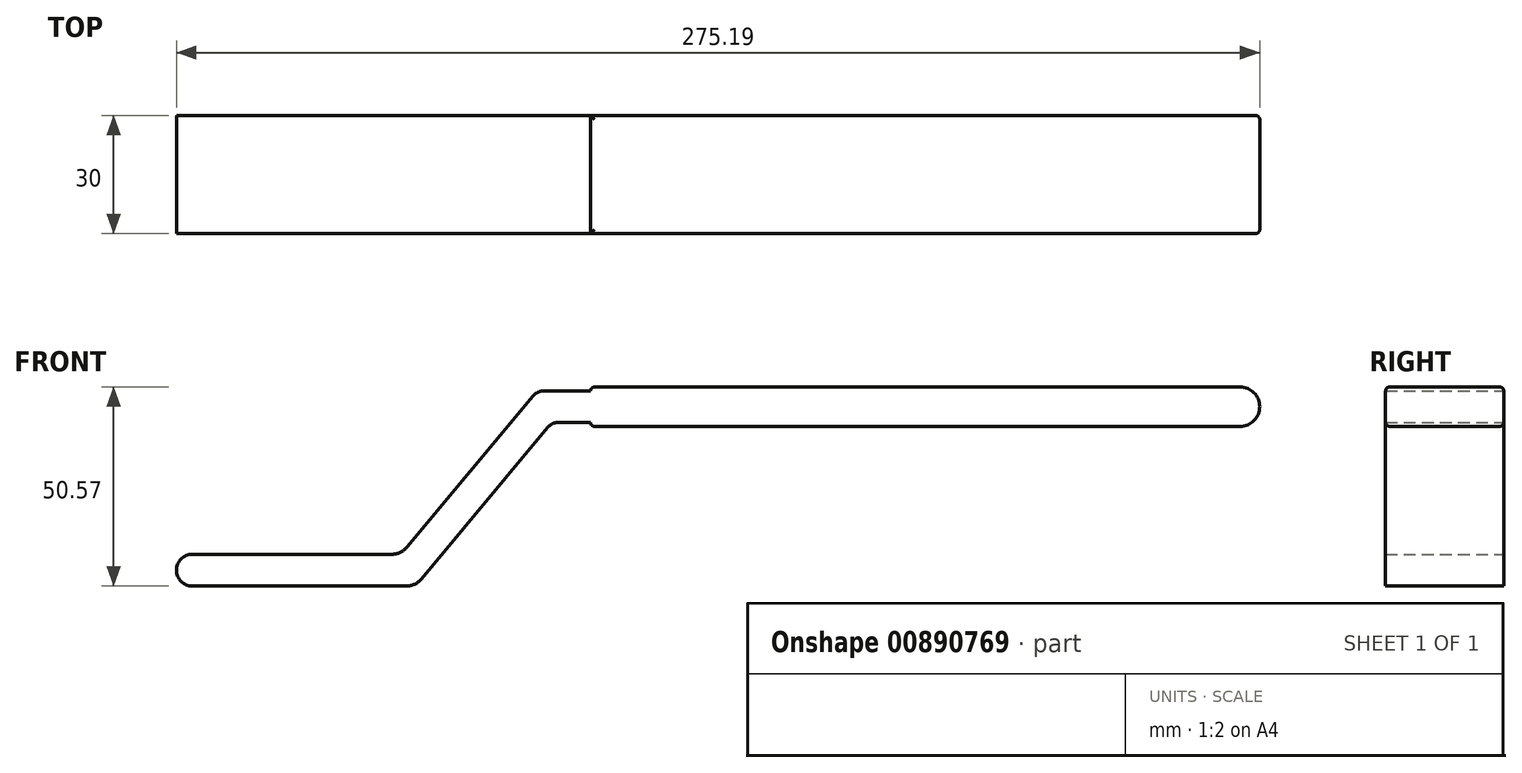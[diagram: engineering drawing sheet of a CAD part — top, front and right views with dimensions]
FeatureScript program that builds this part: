
annotation { "Feature Type Name" : "Feature", "Feature Type Description" : "" }
export const myFeature = defineFeature(function(context is Context, id is Id, definition is map)
    precondition{}
    {
        {
            var Q0;
            Q0=qCreatedBy(makeId("Front.planeOp"),FACE);
            var sketch = newSketch(context, id + "F0", { "sketchPlane" : qUnion([Q0])});
            skLineSegment(sketch, "E0", {"start": v(-114.33, 20.8) * mm, "end": v(-63.67, 20.8) * mm});
            skLineSegment(sketch, "E1", {"start": v(-59.83, 22.6) * mm, "end": v(-27.81, 61.04) * mm});
            skLineSegment(sketch, "E2.0", {"start": v(-56.15, 14.53) * mm, "end": v(-24.07, 53.04) * mm});
            skLineSegment(sketch, "E3.0", {"start": v(-21.38, 54.3) * mm, "end": v(-13.18, 54.3) * mm});
            skLineSegment(sketch, "E4", {"start": v(-114.33, 12.73) * mm, "end": v(-59.99, 12.73) * mm});
            skArc(sketch, "E5", {"start": v(-114.33, 20.8) * mm, "mid": v(-118.37, 16.77) * mm, "end": v(-114.33, 12.73) * mm});
            skPoint(sketch, "E6.visualSharp", {"position": v(-61.33, 20.8) * mm});
            skArc(sketch, "E6.filletArc", {"start": v(-63.67, 20.8) * mm, "mid": v(-61.55, 21.28) * mm, "end": v(-59.83, 22.6) * mm});
            skPoint(sketch, "E7.visualSharp", {"position": v(-57.65, 12.73) * mm});
            skArc(sketch, "E7.filletArc", {"start": v(-59.99, 12.73) * mm, "mid": v(-57.87, 13.2) * mm, "end": v(-56.15, 14.53) * mm});
            skPoint(sketch, "E8.newPointA", {"position": v(-23.08, 54.22) * mm});
            skPoint(sketch, "E8.newPointB", {"position": v(-23.18, 54.3) * mm});
            skArc(sketch, "E8.filletArc", {"start": v(-21.38, 54.3) * mm, "mid": v(-22.86, 53.97) * mm, "end": v(-24.07, 53.04) * mm});
            skPoint(sketch, "E9.visualSharp", {"position": v(-26.76, 62.3) * mm});
            skArc(sketch, "E9.filletArc", {"start": v(-25.12, 62.3) * mm, "mid": v(-26.6, 61.97) * mm, "end": v(-27.81, 61.04) * mm});
            skLineSegment(sketch, "E10", {"start": v(-13.18, 54.3) * mm, "end": v(-13.18, 62.3) * mm});
            skLineSegment(sketch, "E11", {"start": v(-13.18, 62.3) * mm, "end": v(-25.12, 62.3) * mm});
            skLineSegment(sketch, "E12", {"start": v(-13.18, 62.3) * mm, "end": v(-13.18, 63.3) * mm});
            skLineSegment(sketch, "E13", {"start": v(-13.18, 54.3) * mm, "end": v(-13.18, 53.3) * mm});
            skLineSegment(sketch, "E14", {"start": v(-13.18, 63.3) * mm, "end": v(151.82, 63.3) * mm});
            skLineSegment(sketch, "E15", {"start": v(-13.18, 53.3) * mm, "end": v(151.82, 53.3) * mm});
            skArc(sketch, "E16", {"start": v(151.82, 63.3) * mm, "mid": v(156.82, 58.3) * mm, "end": v(151.82, 53.3) * mm});
            skSolve(sketch);
        }
        {
            var Q0;
            Q0=makeQuery(id+"F0.imprint","IMPRINT",FACE,{"disambiguationData":[TD([[makeQuery(id+"F0.imprint","IMPRINT",EDGE,{"derivedFrom":sQuery(id+"F0.wireOp",EDGE,"E0")}),-1.0]])]});
            var Q1;
            Q1=makeQuery(id+"F0.imprint","IMPRINT",FACE,{"disambiguationData":[TD([[makeQuery(id+"F0.imprint","IMPRINT",EDGE,{"derivedFrom":sQuery(id+"F0.wireOp",EDGE,"E10")}),-1.0]])]});
            extrude(context, id + "F1", {"entities" : qUnion([Q0, Q1]), "depth" : 30 * mm, "offsetDistance" : 25.4 * mm});
        }
        {
            var Q0;
            Q0=makeQuery(id+"F1.opExtrude","CAP_EDGE",EDGE,{"disambiguationData":[OSD([sQuery(id+"F0.wireOp",EDGE,"E14")])],"isStart":true});
            var Q1;
            Q1=makeQuery(id+"F1.opExtrude","CAP_EDGE",EDGE,{"disambiguationData":[OSD([sQuery(id+"F0.wireOp",EDGE,"E15")])],"isStart":false});
            var Q2;
            Q2=makeQuery(id+"F1.opExtrude","SWEPT_EDGE",EDGE,{"disambiguationData":[OSD([sQuery(id+"F0.wireOp",EDGE,"E14"),sQuery(id+"F0.wireOp",EDGE,"E16")])]});
            var Q3;
            Q3=makeQuery(id+"F1.opExtrude","SWEPT_EDGE",EDGE,{"disambiguationData":[OSD([sQuery(id+"F0.wireOp",EDGE,"E15"),sQuery(id+"F0.wireOp",EDGE,"E16")])]});
            var Q4;
            Q4=makeQuery(id+"F1.opExtrude","SWEPT_EDGE",EDGE,{"disambiguationData":[OSD([sQuery(id+"F0.wireOp",EDGE,"E13"),sQuery(id+"F0.wireOp",EDGE,"E15")])]});
            var Q5;
            Q5=makeQuery(id+"F1.opExtrude","SWEPT_EDGE",EDGE,{"disambiguationData":[OSD([sQuery(id+"F0.wireOp",EDGE,"E12"),sQuery(id+"F0.wireOp",EDGE,"E14")])]});
            fillet(context, id + "F2", {"entities" : qUnion([Q0, Q1, Q2, Q3, Q4, Q5]), "radius" : 1 * mm, "tangentPropagation" : true, "allowEdgeOverflow" : false});
        }
    });
